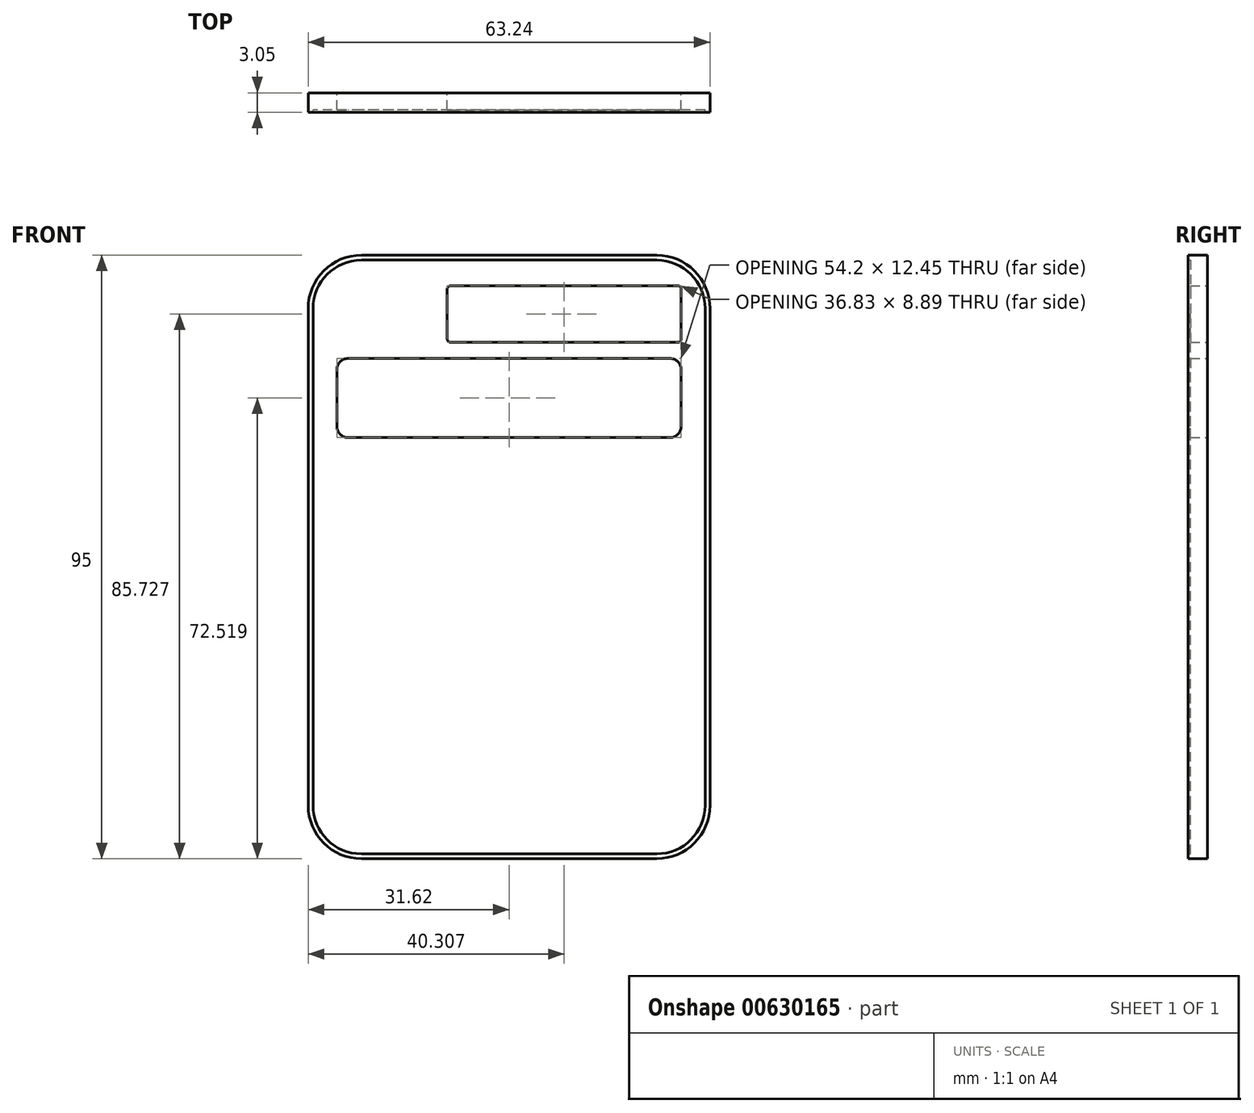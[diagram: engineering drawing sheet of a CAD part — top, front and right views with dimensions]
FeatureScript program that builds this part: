
annotation { "Feature Type Name" : "Feature", "Feature Type Description" : "" }
export const myFeature = defineFeature(function(context is Context, id is Id, definition is map)
    precondition{}
    {
        {
            var Q0;
            Q0=qCreatedBy(makeId("Front.planeOp"),FACE);
            var sketch = newSketch(context, id + "F0", { "sketchPlane" : qUnion([Q0])});
            skLineSegment(sketch, "E0.bottom", {"start": v(23.24, -46.74) * mm, "end": v(-23.24, -46.74) * mm});
            skLineSegment(sketch, "E0.top", {"start": v(23.24, 46.74) * mm, "end": v(-23.24, 46.74) * mm});
            skLineSegment(sketch, "E0.left", {"start": v(30.86, -39.12) * mm, "end": v(30.86, 39.12) * mm});
            skLineSegment(sketch, "E0.right", {"start": v(-30.86, -39.12) * mm, "end": v(-30.86, 39.12) * mm});
            skPoint(sketch, "E0.middle", {"position": v(0, 0) * mm});
            skPoint(sketch, "E1.visualSharp", {"position": v(-30.86, 46.74) * mm});
            skArc(sketch, "E1.filletArc", {"start": v(-23.24, 46.74) * mm, "mid": v(-28.63, 44.5) * mm, "end": v(-30.86, 39.12) * mm});
            skPoint(sketch, "E2.visualSharp", {"position": v(30.86, 46.74) * mm});
            skArc(sketch, "E2.filletArc", {"start": v(30.86, 39.12) * mm, "mid": v(28.63, 44.5) * mm, "end": v(23.24, 46.74) * mm});
            skPoint(sketch, "E3.visualSharp", {"position": v(-30.86, -46.74) * mm});
            skArc(sketch, "E3.filletArc", {"start": v(-30.86, -39.12) * mm, "mid": v(-28.63, -44.5) * mm, "end": v(-23.24, -46.74) * mm});
            skPoint(sketch, "E4.visualSharp", {"position": v(30.86, -46.74) * mm});
            skArc(sketch, "E4.filletArc", {"start": v(23.24, -46.74) * mm, "mid": v(28.63, -44.5) * mm, "end": v(30.86, -39.12) * mm});
            skArc(sketch, "E5.0", {"start": v(-31.62, -39.12) * mm, "mid": v(-29.17, -45.04) * mm, "end": v(-23.24, -47.5) * mm});
            skLineSegment(sketch, "E5.1", {"start": v(23.24, -47.5) * mm, "end": v(-23.24, -47.5) * mm});
            skLineSegment(sketch, "E5.2", {"start": v(-31.62, -39.12) * mm, "end": v(-31.62, 39.12) * mm});
            skArc(sketch, "E5.3", {"start": v(23.24, -47.5) * mm, "mid": v(29.17, -45.04) * mm, "end": v(31.62, -39.12) * mm});
            skArc(sketch, "E5.4", {"start": v(-23.24, 47.5) * mm, "mid": v(-29.17, 45.04) * mm, "end": v(-31.62, 39.12) * mm});
            skLineSegment(sketch, "E5.5", {"start": v(23.24, 47.5) * mm, "end": v(-23.24, 47.5) * mm});
            skArc(sketch, "E5.6", {"start": v(31.62, 39.12) * mm, "mid": v(29.17, 45.04) * mm, "end": v(23.24, 47.5) * mm});
            skLineSegment(sketch, "E5.7", {"start": v(31.62, -39.12) * mm, "end": v(31.62, 39.12) * mm});
            skLineSegment(sketch, "E6.bottom", {"start": v(25.32, 18.8) * mm, "end": v(-25.32, 18.8) * mm});
            skLineSegment(sketch, "E6.top", {"start": v(25.32, 31.24) * mm, "end": v(-25.32, 31.24) * mm});
            skLineSegment(sketch, "E6.left", {"start": v(27.1, 20.57) * mm, "end": v(27.1, 29.46) * mm});
            skLineSegment(sketch, "E6.right", {"start": v(-27.1, 20.57) * mm, "end": v(-27.1, 29.46) * mm});
            skPoint(sketch, "E6.middle", {"position": v(0, 25.02) * mm});
            skPoint(sketch, "E7.visualSharp", {"position": v(27.1, 31.24) * mm});
            skArc(sketch, "E7.filletArc", {"start": v(27.1, 29.46) * mm, "mid": v(26.58, 30.72) * mm, "end": v(25.32, 31.24) * mm});
            skPoint(sketch, "E8.visualSharp", {"position": v(27.1, 18.8) * mm});
            skArc(sketch, "E8.filletArc", {"start": v(25.32, 18.8) * mm, "mid": v(26.58, 19.32) * mm, "end": v(27.1, 20.57) * mm});
            skPoint(sketch, "E9.visualSharp", {"position": v(-27.1, 18.8) * mm});
            skArc(sketch, "E9.filletArc", {"start": v(-27.1, 20.57) * mm, "mid": v(-26.58, 19.32) * mm, "end": v(-25.32, 18.8) * mm});
            skPoint(sketch, "E10.visualSharp", {"position": v(-27.1, 31.24) * mm});
            skArc(sketch, "E10.filletArc", {"start": v(-25.32, 31.24) * mm, "mid": v(-26.58, 30.72) * mm, "end": v(-27.1, 29.46) * mm});
            skLineSegment(sketch, "E11.bottom", {"start": v(-9.22, 42.67) * mm, "end": v(26.6, 42.67) * mm});
            skLineSegment(sketch, "E11.top", {"start": v(-9.22, 33.78) * mm, "end": v(26.6, 33.78) * mm});
            skLineSegment(sketch, "E11.left", {"start": v(-9.73, 42.16) * mm, "end": v(-9.73, 34.3) * mm});
            skLineSegment(sketch, "E11.right", {"start": v(27.1, 42.16) * mm, "end": v(27.1, 34.3) * mm});
            skPoint(sketch, "E12.visualSharp", {"position": v(-9.73, 42.67) * mm});
            skArc(sketch, "E12.filletArc", {"start": v(-9.22, 42.67) * mm, "mid": v(-9.58, 42.52) * mm, "end": v(-9.73, 42.16) * mm});
            skPoint(sketch, "E13.visualSharp", {"position": v(-9.73, 33.78) * mm});
            skArc(sketch, "E13.filletArc", {"start": v(-9.73, 34.3) * mm, "mid": v(-9.58, 33.93) * mm, "end": v(-9.22, 33.78) * mm});
            skPoint(sketch, "E14.visualSharp", {"position": v(27.1, 33.78) * mm});
            skArc(sketch, "E14.filletArc", {"start": v(26.6, 33.78) * mm, "mid": v(26.95, 33.93) * mm, "end": v(27.1, 34.3) * mm});
            skPoint(sketch, "E15.visualSharp", {"position": v(27.1, 42.67) * mm});
            skArc(sketch, "E15.filletArc", {"start": v(27.1, 42.16) * mm, "mid": v(26.95, 42.52) * mm, "end": v(26.6, 42.67) * mm});
            skSolve(sketch);
        }
        {
            var Q0;
            Q0=makeQuery(id+"F0.imprint","IMPRINT",FACE,{"disambiguationData":[TD([[makeQuery(id+"F0.imprint","IMPRINT",EDGE,{"derivedFrom":sQuery(id+"F0.wireOp",EDGE,"E0.bottom")}),1.0]])]});
            extrude(context, id + "F1", {"entities" : qUnion([Q0]), "depth" : 3.05 * mm, "offsetDistance" : 25.4 * mm});
        }
        {
            var Q0;
            Q0=makeQuery(id+"F0.imprint","IMPRINT",FACE,{"disambiguationData":[TD([[makeQuery(id+"F0.imprint","IMPRINT",EDGE,{"derivedFrom":sQuery(id+"F0.wireOp",EDGE,"E0.bottom")}),-1.0]])]});
            extrude(context, id + "F2", {"entities" : qUnion([Q0]), "operationType" : NewBodyOperationType.ADD, "depth" : 2.67 * mm, "offsetDistance" : 25.4 * mm});
        }
    });
